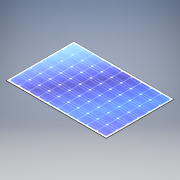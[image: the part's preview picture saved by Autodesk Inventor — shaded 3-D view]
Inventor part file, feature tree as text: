
AUTODESK INVENTOR PART (.ipt)
format: ipt  version: 2017 (Build 210142000, 142)  size: 293,888 bytes
history: native  units: in
note: dims shown in document units (in); Inventor stores cm internally (conversion verified against a paired STEP export)
features: sketch x2, other x2, fillet x2, extrude x1, chamfer x1
ambient origin geometry x8: Origin, YZ Plane, XZ Plane, XY Plane, X Axis, Y Axis, Z Axis, Center Point
bodies: Solid1 (feature_tree)
feature tree (8):
  sketch  "Sketch1"  dims[d1=0.125in d2=0.0in d3=0.025in d4=0.125in d5=45.0deg]
  extrude  "Extrusion1"  Depth=0.025in TaperAngle=45.0deg
  other  "Decal1"
  chamfer  "Chamfer1"  Distance=0.001in
  fillet  "Fillet1"  Radius=16.8986in
  fillet  "Fillet2"  Radius=24.9967in
  other  "Image1"
  sketch  "Sketch2"  dims[d6=0.025in d7=0.001in d8=16.8986in d9=24.9967in]
